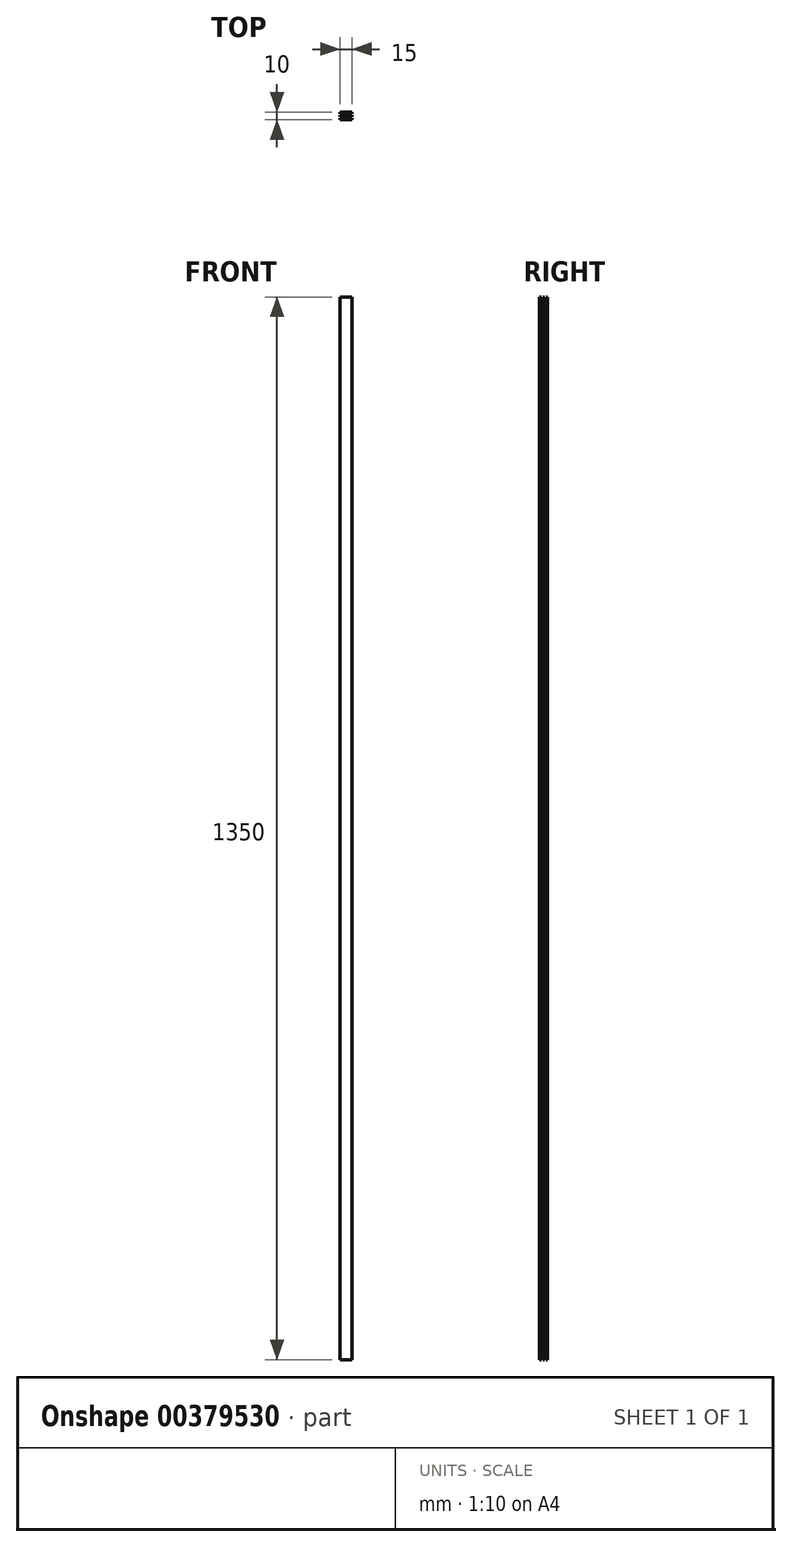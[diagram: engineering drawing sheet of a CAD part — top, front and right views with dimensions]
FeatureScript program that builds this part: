
annotation { "Feature Type Name" : "Feature", "Feature Type Description" : "" }
export const myFeature = defineFeature(function(context is Context, id is Id, definition is map)
    precondition{}
    {
        {
            var Q0;
            Q0=qCreatedBy(makeId("Top.planeOp"),FACE);
            var sketch = newSketch(context, id + "F0", { "sketchPlane" : qUnion([Q0])});
            skLineSegment(sketch, "E0", {"start": v(0, 0) * mm, "end": v(0, 8.82) * mm, "construction": true});
            skLineSegment(sketch, "E1", {"start": v(0, 8.82) * mm, "end": v(-15, 8.82) * mm});
            skLineSegment(sketch, "E2", {"start": v(-15, 8.82) * mm, "end": v(-15, 6.82) * mm});
            skLineSegment(sketch, "E3", {"start": v(-15, 6.82) * mm, "end": v(0, 6.82) * mm});
            skLineSegment(sketch, "E4", {"start": v(0, 6.82) * mm, "end": v(0, 4.82) * mm});
            skLineSegment(sketch, "E5", {"start": v(0, 4.82) * mm, "end": v(-15, 4.82) * mm});
            skLineSegment(sketch, "E6", {"start": v(-15, 4.82) * mm, "end": v(-15, 2.82) * mm});
            skLineSegment(sketch, "E7", {"start": v(-15, 2.82) * mm, "end": v(0, 2.82) * mm});
            skLineSegment(sketch, "E8", {"start": v(0, 2.82) * mm, "end": v(0, 0.82) * mm});
            skLineSegment(sketch, "E9", {"start": v(0, 0.82) * mm, "end": v(-15, 0.82) * mm});
            skLineSegment(sketch, "E10", {"start": v(-15, 0.82) * mm, "end": v(-15, -1.18) * mm});
            skLineSegment(sketch, "E11", {"start": v(-15, -1.18) * mm, "end": v(0, -1.18) * mm});
            skLineSegment(sketch, "E12", {"start": v(0, 8.82) * mm, "end": v(0, -1.18) * mm});
            skSolve(sketch);
        }
        {
            var Q0;
            {var subQ0=sQuery(id+"F0.wireOp",EDGE,"E1");Q0=makeQuery(id+"F0.imprint","IMPRINT",FACE,{"disambiguationData":[TD([[makeQuery(id+"F0.imprint","IMPRINT",EDGE,{"derivedFrom":subQ0}),1.0]])]});}
            var Q1;
            {var subQ0=sQuery(id+"F0.wireOp",EDGE,"E5");Q1=makeQuery(id+"F0.imprint","IMPRINT",FACE,{"disambiguationData":[TD([[makeQuery(id+"F0.imprint","IMPRINT",EDGE,{"derivedFrom":subQ0}),1.0]])]});}
            var Q2;
            {var subQ0=sQuery(id+"F0.wireOp",EDGE,"E9");Q2=makeQuery(id+"F0.imprint","IMPRINT",FACE,{"disambiguationData":[TD([[makeQuery(id+"F0.imprint","IMPRINT",EDGE,{"derivedFrom":subQ0}),1.0]])]});}
            extrude(context, id + "F1", {"entities" : qUnion([Q0, Q1, Q2]), "depth" : (150 * 9) * mm});
        }
    });
